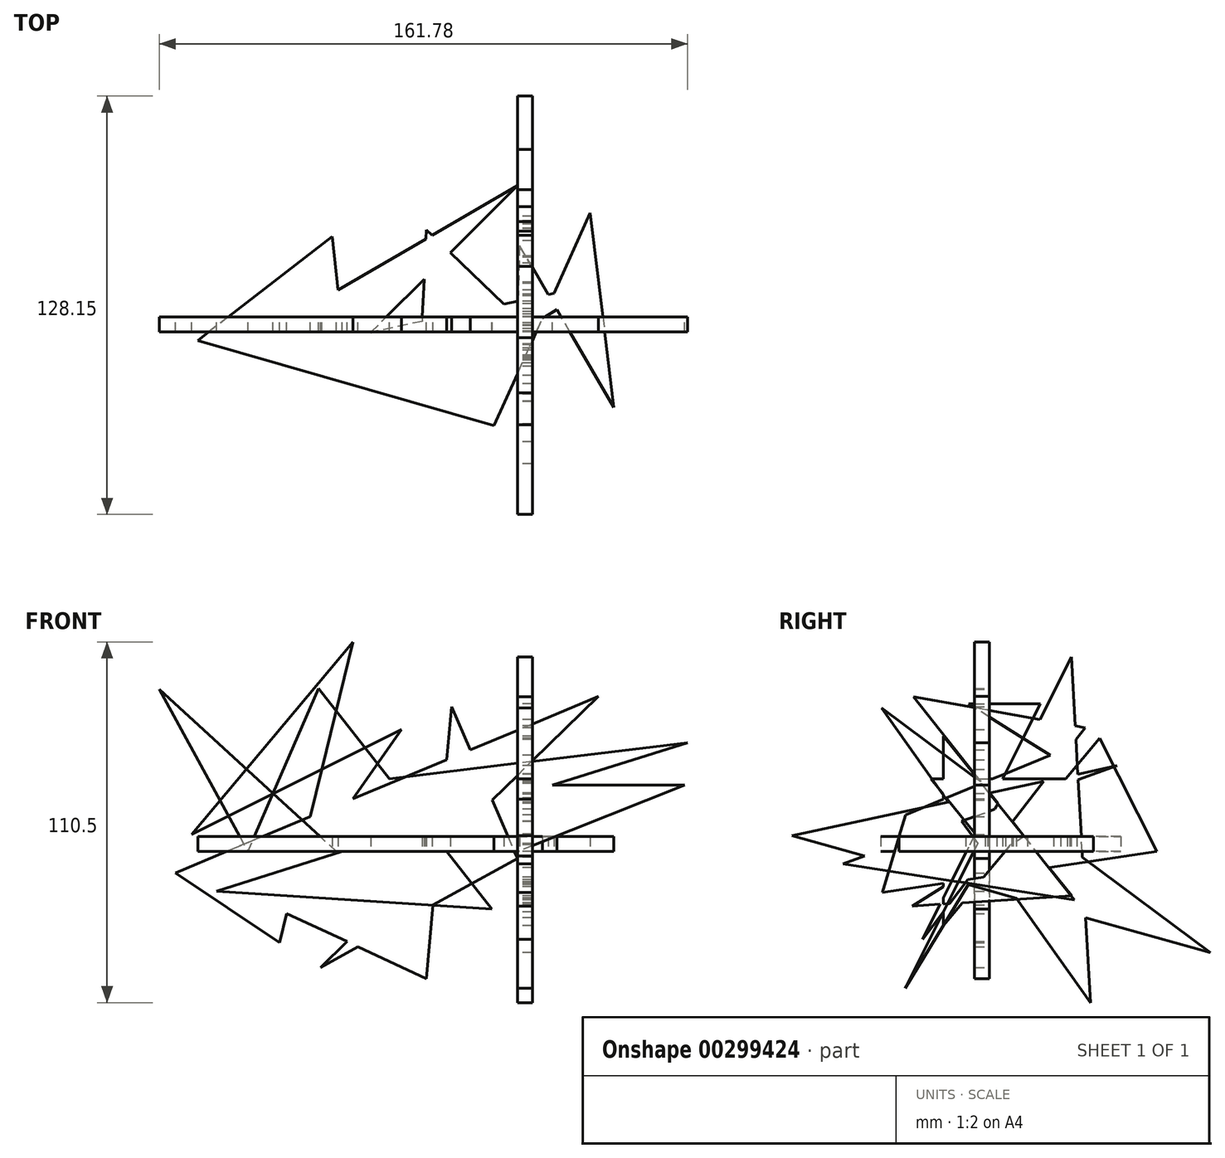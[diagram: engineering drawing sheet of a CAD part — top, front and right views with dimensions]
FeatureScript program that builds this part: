
annotation { "Feature Type Name" : "Feature", "Feature Type Description" : "" }
export const myFeature = defineFeature(function(context is Context, id is Id, definition is map)
    precondition{}
    {
        {
            var Q0;
            Q0=qCreatedBy(makeId("Front.planeOp"),FACE);
            var sketch = newSketch(context, id + "F0", { "sketchPlane" : qUnion([Q0])});
            skLineSegment(sketch, "E0", {"start": v(0, 0) * mm, "end": v(-55.44, 0) * mm});
            skLineSegment(sketch, "E1", {"start": v(-55.44, 20.3) * mm, "end": v(51.2, 20.3) * mm});
            skLineSegment(sketch, "E2", {"start": v(51.2, 20.3) * mm, "end": v(0, 0) * mm});
            skLineSegment(sketch, "E3", {"start": v(-55.44, 0) * mm, "end": v(-109.67, 49.69) * mm});
            skLineSegment(sketch, "E4", {"start": v(-109.67, 49.69) * mm, "end": v(-82.56, 0) * mm});
            skPoint(sketch, "E4.endSnap0", {"position": v(-82.56, 24.84) * mm});
            skLineSegment(sketch, "E5", {"start": v(-82.56, 0) * mm, "end": v(-60.9, 49.99) * mm});
            skLineSegment(sketch, "E6", {"start": v(-60.9, 49.99) * mm, "end": v(-7.88, -17.57) * mm});
            skLineSegment(sketch, "E7", {"start": v(-7.88, -17.57) * mm, "end": v(-92.1, -12.12) * mm});
            skLineSegment(sketch, "E8", {"start": v(-92.1, -12.12) * mm, "end": v(52.1, 33.33) * mm});
            skLineSegment(sketch, "E9", {"start": v(52.1, 33.33) * mm, "end": v(-55.44, 20.3) * mm});
            skSolve(sketch);
        }
        {
            var Q0;
            Q0=qCreatedBy(makeId("Top.planeOp"),FACE);
            var sketch = newSketch(context, id + "F1", { "sketchPlane" : qUnion([Q0])});
            skLineSegment(sketch, "E10", {"start": v(0, 0) * mm, "end": v(-27.9, 26.75) * mm});
            skLineSegment(sketch, "E11", {"start": v(-27.9, 26.75) * mm, "end": v(-30.23, -24.89) * mm});
            skLineSegment(sketch, "E12", {"start": v(-30.23, -24.89) * mm, "end": v(23.97, 10) * mm});
            skLineSegment(sketch, "E13", {"start": v(23.97, 10) * mm, "end": v(-44.88, -4.65) * mm});
            skLineSegment(sketch, "E14", {"start": v(-44.88, -4.65) * mm, "end": v(0, 40.24) * mm});
            skLineSegment(sketch, "E15", {"start": v(0, 40.24) * mm, "end": v(-83.95, -8.6) * mm});
            skLineSegment(sketch, "E16", {"start": v(-83.95, -8.6) * mm, "end": v(-52.83, -10) * mm});
            skLineSegment(sketch, "E17", {"start": v(-52.83, -10) * mm, "end": v(-56.74, 24.65) * mm});
            skLineSegment(sketch, "E18", {"start": v(-56.74, 24.65) * mm, "end": v(-97.9, -7.21) * mm});
            skLineSegment(sketch, "E19", {"start": v(-97.9, -7.21) * mm, "end": v(-7.2, -33.26) * mm});
            skLineSegment(sketch, "E20", {"start": v(-7.2, -33.26) * mm, "end": v(22.34, 31.86) * mm});
            skLineSegment(sketch, "E21", {"start": v(22.34, 31.86) * mm, "end": v(29.55, -27.68) * mm});
            skLineSegment(sketch, "E22", {"start": v(29.55, -27.68) * mm, "end": v(0.71, 21.89) * mm});
            skLineSegment(sketch, "E23", {"start": v(0.71, 21.89) * mm, "end": v(0, 0) * mm});
            skSolve(sketch);
        }
        {
            var Q0;
            Q0=qCreatedBy(makeId("Right.planeOp"),FACE);
            var sketch = newSketch(context, id + "F2", { "sketchPlane" : qUnion([Q0])});
            skLineSegment(sketch, "E24", {"start": v(0, 0) * mm, "end": v(-17.85, 22.2) * mm});
            skLineSegment(sketch, "E25", {"start": v(-17.85, 22.2) * mm, "end": v(39.06, 22.2) * mm});
            skLineSegment(sketch, "E26", {"start": v(39.06, 22.2) * mm, "end": v(-23.6, -16.7) * mm});
            skLineSegment(sketch, "E27", {"start": v(-23.6, -16.7) * mm, "end": v(25.22, -13.56) * mm});
            skLineSegment(sketch, "E28", {"start": v(25.22, -13.56) * mm, "end": v(-14.11, 35.38) * mm});
            skLineSegment(sketch, "E29", {"start": v(-14.11, 35.38) * mm, "end": v(-14.11, -22.7) * mm});
            skLineSegment(sketch, "E30", {"start": v(-14.11, -22.7) * mm, "end": v(33.84, 34.74) * mm});
            skLineSegment(sketch, "E31", {"start": v(33.84, 34.74) * mm, "end": v(51.33, 0) * mm});
            skLineSegment(sketch, "E32", {"start": v(51.33, 0) * mm, "end": v(-32.73, -12.51) * mm});
            skLineSegment(sketch, "E33", {"start": v(-32.73, -12.51) * mm, "end": v(-25.69, 11.24) * mm});
            skLineSegment(sketch, "E34", {"start": v(-25.69, 11.24) * mm, "end": v(18.7, 29.52) * mm});
            skLineSegment(sketch, "E35", {"start": v(18.7, 29.52) * mm, "end": v(-6.37, 45.18) * mm});
            skLineSegment(sketch, "E36", {"start": v(-6.37, 45.18) * mm, "end": v(15.56, 45.18) * mm});
            skLineSegment(sketch, "E37", {"start": v(15.56, 45.18) * mm, "end": v(-20.46, -26.87) * mm});
            skLineSegment(sketch, "E38", {"start": v(-20.46, -26.87) * mm, "end": v(0, 0) * mm});
            skSolve(sketch);
        }
        {
            var Q0;
            Q0 = qSketchRegion(id + "F0", true);
            extrude(context, id + "F3", {"entities" : qUnion([Q0]), "depth" : 4.57 * mm});
        }
        {
            var Q0;
            Q0 = qSketchRegion(id + "F1", true);
            extrude(context, id + "F4", {"entities" : qUnion([Q0]), "depth" : 4.57 * mm});
        }
        {
            var Q0;
            Q0 = qSketchRegion(id + "F2", true);
            extrude(context, id + "F5", {"entities" : qUnion([Q0]), "depth" : 4.57 * mm});
        }
        {
            var Q0;
            Q0=qCreatedBy(makeId("Front.planeOp"),FACE);
            var sketch = newSketch(context, id + "F6", { "sketchPlane" : qUnion([Q0])});
            skLineSegment(sketch, "E39", {"start": v(-35.5, 37.33) * mm, "end": v(-73.88, -17.5) * mm});
            skLineSegment(sketch, "E40", {"start": v(-73.88, -17.5) * mm, "end": v(-27.93, -38.9) * mm});
            skLineSegment(sketch, "E41", {"start": v(-27.93, -38.9) * mm, "end": v(-20.1, 44.38) * mm});
            skLineSegment(sketch, "E42", {"start": v(-20.1, 44.38) * mm, "end": v(0, -2.09) * mm});
            skLineSegment(sketch, "E43", {"start": v(0, -2.09) * mm, "end": v(-60.3, -35.5) * mm});
            skLineSegment(sketch, "E44", {"start": v(-60.3, -35.5) * mm, "end": v(24.8, 47.51) * mm});
            skLineSegment(sketch, "E45", {"start": v(24.8, 47.51) * mm, "end": v(-104.69, -6.53) * mm});
            skLineSegment(sketch, "E46", {"start": v(-104.69, -6.53) * mm, "end": v(-72.84, -27.93) * mm});
            skLineSegment(sketch, "E47", {"start": v(-72.84, -27.93) * mm, "end": v(-50.39, 64.22) * mm});
            skLineSegment(sketch, "E48", {"start": v(-50.39, 64.22) * mm, "end": v(-99.73, 5.22) * mm});
            skLineSegment(sketch, "E49", {"start": v(-99.73, 5.22) * mm, "end": v(-35.5, 37.33) * mm});
            skSolve(sketch);
        }
        {
            var Q0;
            Q0 = qSketchRegion(id + "F6", true);
            extrude(context, id + "F7", {"entities" : qUnion([Q0]), "depth" : 4.57 * mm});
        }
        {
            var Q0;
            Q0=qCreatedBy(makeId("Right.planeOp"),FACE);
            var sketch = newSketch(context, id + "F8", { "sketchPlane" : qUnion([Q0])});
            skLineSegment(sketch, "E50", {"start": v(0, 0) * mm, "end": v(29.3, 37.91) * mm});
            skLineSegment(sketch, "E51", {"start": v(29.3, 37.91) * mm, "end": v(-23.26, 47.45) * mm});
            skLineSegment(sketch, "E52", {"start": v(-23.26, 47.45) * mm, "end": v(26.05, -14.89) * mm});
            skLineSegment(sketch, "E53", {"start": v(26.05, -14.89) * mm, "end": v(-44.89, -3.72) * mm});
            skLineSegment(sketch, "E54", {"start": v(-44.89, -3.72) * mm, "end": v(39.07, 26.28) * mm});
            skLineSegment(sketch, "E55", {"start": v(39.07, 26.28) * mm, "end": v(-60.47, 4.88) * mm});
            skLineSegment(sketch, "E56", {"start": v(-60.47, 4.88) * mm, "end": v(67.68, -30.93) * mm});
            skLineSegment(sketch, "E57", {"start": v(67.68, -30.93) * mm, "end": v(-33.03, 43.96) * mm});
            skLineSegment(sketch, "E58", {"start": v(-33.03, 43.96) * mm, "end": v(30.93, -46.28) * mm});
            skLineSegment(sketch, "E59", {"start": v(30.93, -46.28) * mm, "end": v(25.12, 59.54) * mm});
            skLineSegment(sketch, "E60", {"start": v(25.12, 59.54) * mm, "end": v(-25.82, -41.87) * mm});
            skLineSegment(sketch, "E61", {"start": v(-25.82, -41.87) * mm, "end": v(-1.05, -1.16) * mm});
            skSolve(sketch);
        }
        {
            var Q0;
            Q0 = qSketchRegion(id + "F8", true);
            extrude(context, id + "F9", {"entities" : qUnion([Q0]), "depth" : 4.57 * mm});
        }
    });
